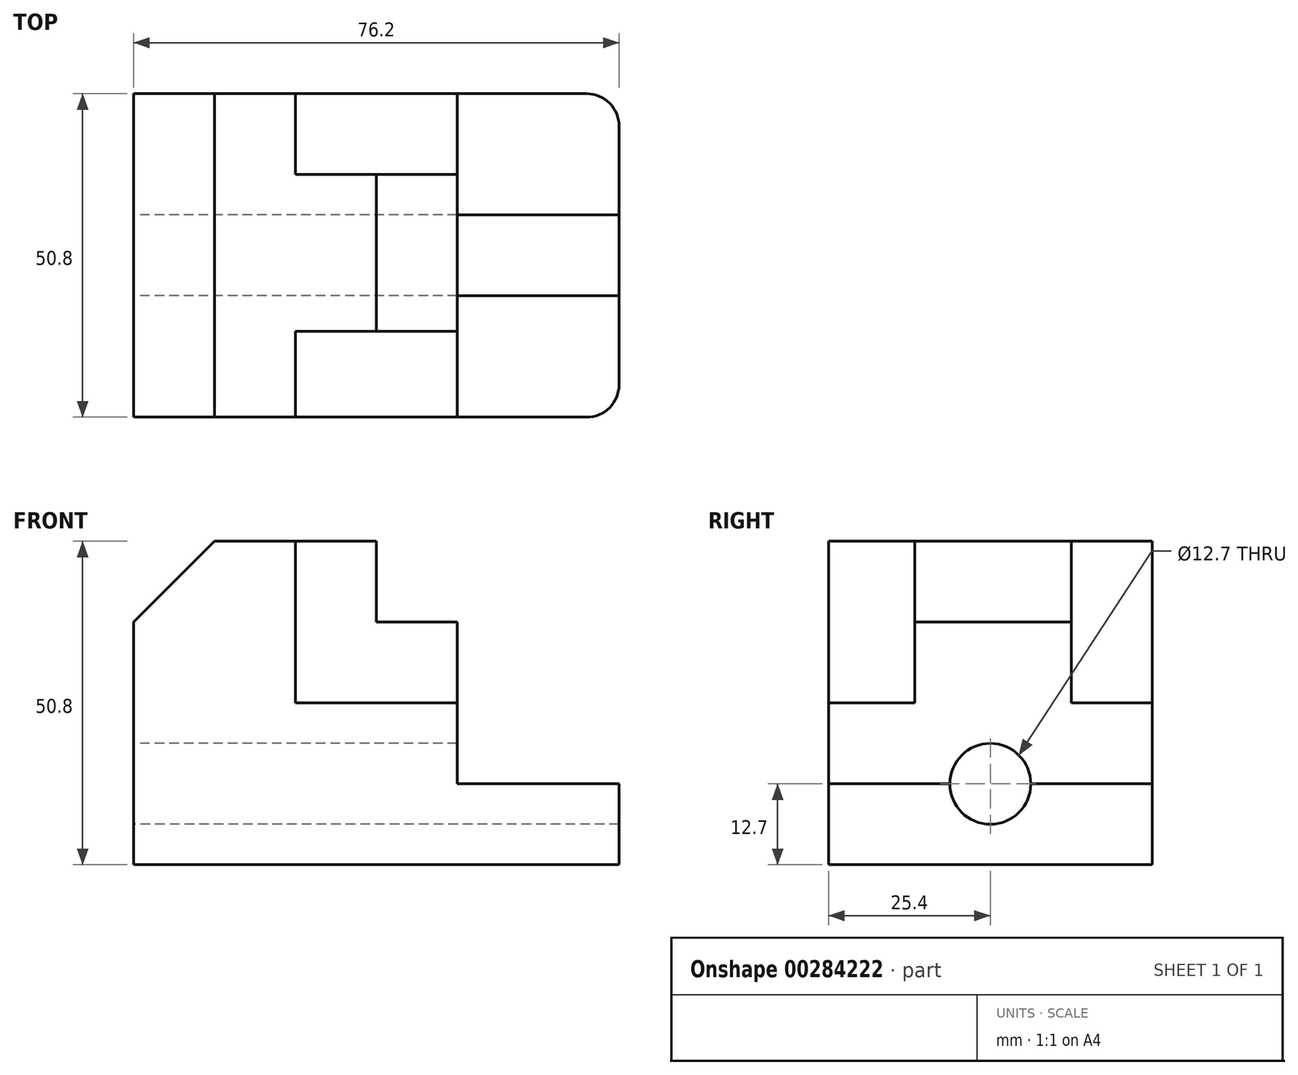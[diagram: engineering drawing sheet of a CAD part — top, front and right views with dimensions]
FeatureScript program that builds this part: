
annotation { "Feature Type Name" : "Feature", "Feature Type Description" : "" }
export const myFeature = defineFeature(function(context is Context, id is Id, definition is map)
    precondition{}
    {
        {
            var Q0;
            Q0=qCreatedBy(makeId("Front.planeOp"),FACE);
            var sketch = newSketch(context, id + "F0", { "sketchPlane" : qUnion([Q0])});
            skLineSegment(sketch, "E0", {"start": v(0, 0) * mm, "end": v(0, 38.1) * mm});
            skLineSegment(sketch, "E1", {"start": v(0, 38.1) * mm, "end": v(12.7, 50.8) * mm});
            skLineSegment(sketch, "E2", {"start": v(12.7, 50.8) * mm, "end": v(38.1, 50.8) * mm});
            skLineSegment(sketch, "E3", {"start": v(38.1, 50.8) * mm, "end": v(38.1, 38.1) * mm});
            skLineSegment(sketch, "E4", {"start": v(38.1, 38.1) * mm, "end": v(50.8, 38.1) * mm});
            skLineSegment(sketch, "E5", {"start": v(50.8, 38.1) * mm, "end": v(50.8, 12.7) * mm});
            skLineSegment(sketch, "E6", {"start": v(50.8, 12.7) * mm, "end": v(76.2, 12.7) * mm});
            skLineSegment(sketch, "E7", {"start": v(76.2, 12.7) * mm, "end": v(76.2, 0) * mm});
            skLineSegment(sketch, "E8", {"start": v(76.2, 0) * mm, "end": v(0, 0) * mm});
            skLineSegment(sketch, "E9", {"start": v(25.4, 50.8) * mm, "end": v(25.4, 25.4) * mm});
            skLineSegment(sketch, "E10", {"start": v(25.4, 25.4) * mm, "end": v(50.8, 25.4) * mm});
            skSolve(sketch);
        }
        {
            var Q0;
            Q0=makeQuery(id+"F0.imprint","IMPRINT",FACE,{"disambiguationData":[TD([[makeQuery(id+"F0.imprint","IMPRINT",EDGE,{"derivedFrom":sQuery(id+"F0.wireOp",EDGE,"E0")}),-1.0]])]});
            var Q1;
            {var subQ3=sQuery(id+"F0.wireOp",EDGE,"E3");Q1=makeQuery(id+"F0.imprint","IMPRINT",FACE,{"disambiguationData":[TD([[makeQuery(id+"F0.imprint","IMPRINT",EDGE,{"derivedFrom":subQ3}),-1.0]])]});}
            var Q2;
            Q2=sQuery(id+"F0.wireOp",VERTEX,"E0.start");
            extrude(context, id + "F1", {"entities" : qUnion([Q0, Q1]), "endBound" : BoundingType.SYMMETRIC, "endBoundEntityVertex" : qUnion([Q2]), "depth" : 50.8 * mm, "hasSecondDirection" : true, "secondDirectionOppositeDirection" : true, "secondDirectionDepth" : 25.4 * mm});
        }
        {
            var Q0;
            Q0=makeQuery(id+"F1.opExtrude","SWEPT_FACE",FACE,{"disambiguationData":[OSD([sQuery(id+"F0.wireOp",EDGE,"E2")])]});
            var sketch = newSketch(context, id + "F2", { "sketchPlane" : qUnion([Q0])});
            skLineSegment(sketch, "E11.bottom", {"start": v(25.4, 25.4) * mm, "end": v(50.8, 25.4) * mm});
            skLineSegment(sketch, "E11.top", {"start": v(25.4, 12.7) * mm, "end": v(50.8, 12.7) * mm});
            skLineSegment(sketch, "E11.left", {"start": v(25.4, 25.4) * mm, "end": v(25.4, 12.7) * mm});
            skLineSegment(sketch, "E11.right", {"start": v(50.8, 25.4) * mm, "end": v(50.8, 12.7) * mm});
            skLineSegment(sketch, "E12.bottom", {"start": v(25.4, -25.4) * mm, "end": v(50.8, -25.4) * mm});
            skLineSegment(sketch, "E12.top", {"start": v(25.4, -11.89) * mm, "end": v(50.8, -11.89) * mm});
            skLineSegment(sketch, "E12.left", {"start": v(25.4, -25.4) * mm, "end": v(25.4, -11.89) * mm});
            skLineSegment(sketch, "E12.right", {"start": v(50.8, -25.4) * mm, "end": v(50.8, -11.89) * mm});
            skSolve(sketch);
        }
        {
            var Q0;
            {var subQ3=sQuery(id+"F2.wireOp",EDGE,"E11.right");Q0=makeQuery(id+"F2.imprint","IMPRINT",FACE,{"disambiguationData":[TD([[makeQuery(id+"F2.imprint","IMPRINT",EDGE,{"derivedFrom":subQ3}),-1.0]])]});}
            var Q1;
            {var subQ4=sQuery(id+"F2.wireOp",EDGE,"E11.left");Q1=makeQuery(id+"F2.imprint","IMPRINT",FACE,{"disambiguationData":[TD([[makeQuery(id+"F2.imprint","IMPRINT",EDGE,{"derivedFrom":subQ4}),1.0]])]});}
            var Q2;
            {var subQ4=sQuery(id+"F2.wireOp",EDGE,"E12.left");Q2=makeQuery(id+"F2.imprint","IMPRINT",FACE,{"disambiguationData":[TD([[makeQuery(id+"F2.imprint","IMPRINT",EDGE,{"derivedFrom":subQ4}),-1.0]])]});}
            var Q3;
            {var subQ3=sQuery(id+"F2.wireOp",EDGE,"E12.right");Q3=makeQuery(id+"F2.imprint","IMPRINT",FACE,{"disambiguationData":[TD([[makeQuery(id+"F2.imprint","IMPRINT",EDGE,{"derivedFrom":subQ3}),1.0]])]});}
            extrude(context, id + "F3", {"entities" : qUnion([Q0, Q1, Q2, Q3]), "operationType" : NewBodyOperationType.REMOVE, "oppositeDirection" : true, "depth" : 25.4 * mm});
        }
        {
            var Q0;
            Q0=qCreatedBy(makeId("Right.planeOp"),FACE);
            var sketch = newSketch(context, id + "F4", { "sketchPlane" : qUnion([Q0])});
            skCircle(sketch, "E13", {"center": v(0, 12.7) * mm, "radius": 6.35 * mm});
            skSolve(sketch);
        }
        {
            var Q0;
            Q0=makeQuery(id+"F4.imprint","IMPRINT",FACE,{"disambiguationData":[TD([[makeQuery(id+"F4.imprint","IMPRINT",EDGE,{"derivedFrom":sQuery(id+"F4.wireOp",EDGE,"E13")}),1.0]])]});
            var Q1;
            Q1=sQuery(id+"F4.wireOp",EDGE,"E13");
            extrude(context, id + "F5", {"entities" : qUnion([Q0]), "operationType" : NewBodyOperationType.REMOVE, "surfaceEntities" : qUnion([Q1]), "endBound" : BoundingType.THROUGH_ALL, "depth" : 25.4 * mm});
        }
        {
            var Q0;
            Q0=makeQuery(id+"F1.opExtrude","CAP_EDGE",EDGE,{"disambiguationData":[OSD([sQuery(id+"F0.wireOp",EDGE,"E7")])],"isStart":false});
            var Q1;
            Q1=makeQuery(id+"F1.opExtrude","CAP_EDGE",EDGE,{"disambiguationData":[OSD([sQuery(id+"F0.wireOp",EDGE,"E7")])],"isStart":true});
            fillet(context, id + "F6", {"entities" : qUnion([Q0, Q1]), "radius" : 5.08 * mm, "tangentPropagation" : true, "allowEdgeOverflow" : false});
        }
    });
